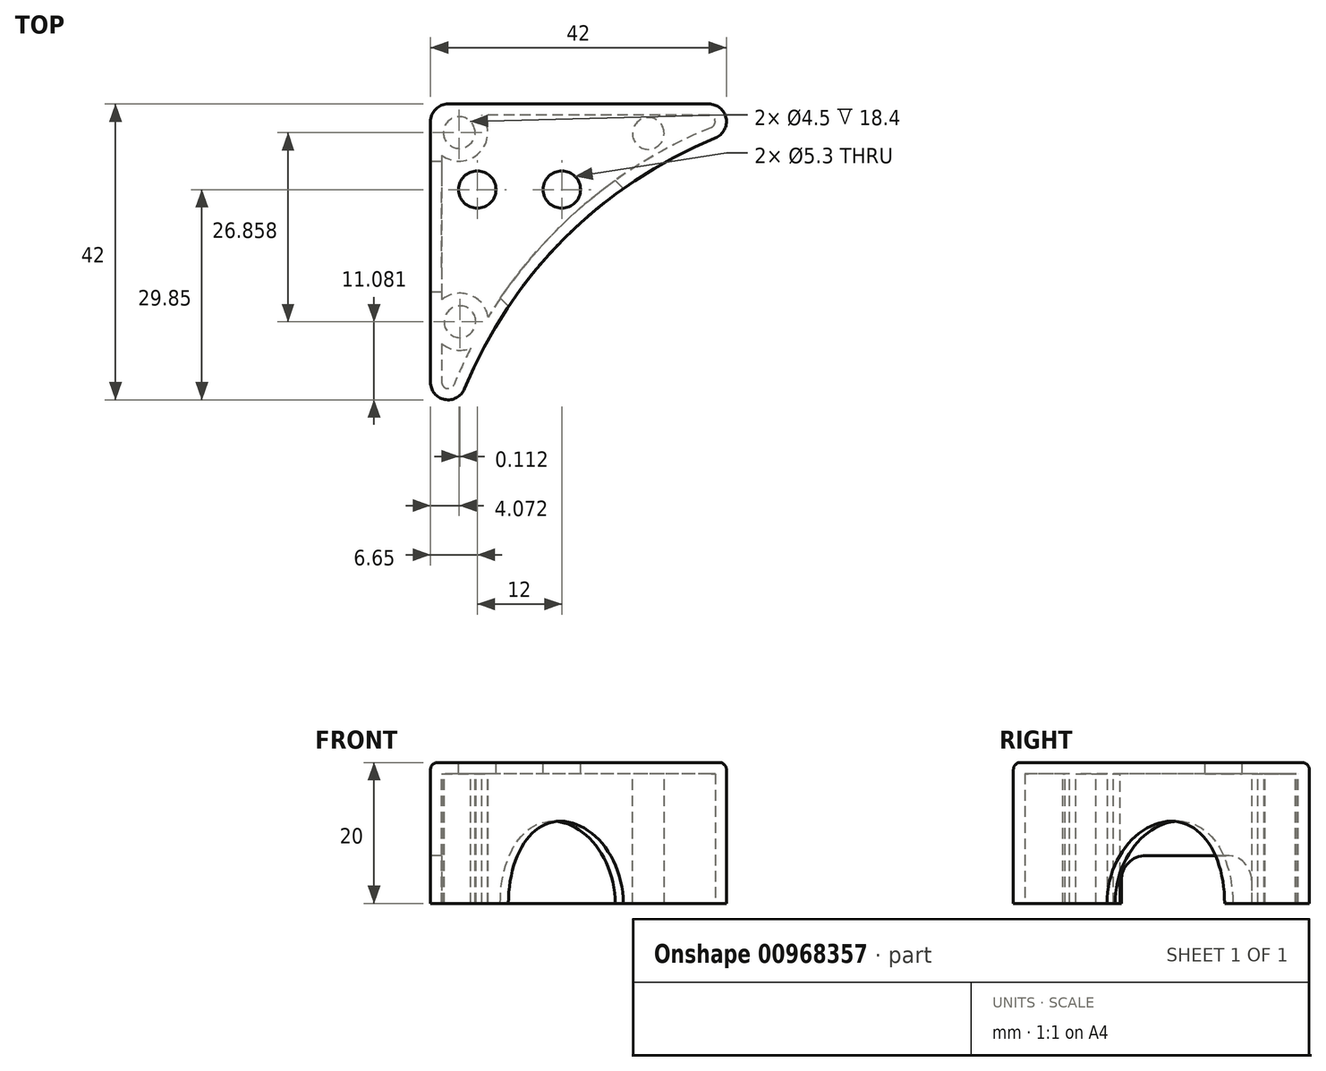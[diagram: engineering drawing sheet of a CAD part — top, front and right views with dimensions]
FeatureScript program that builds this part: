
annotation { "Feature Type Name" : "Feature", "Feature Type Description" : "" }
export const myFeature = defineFeature(function(context is Context, id is Id, definition is map)
    precondition{}
    {
        {
            var Q0;
            Q0=qCreatedBy(makeId("Top.planeOp"),FACE);
            var sketch = newSketch(context, id + "F0", { "sketchPlane" : qUnion([Q0])});
            skCircle(sketch, "E0", {"center": v(0, 0) * mm, "radius": 65 * mm});
            skLineSegment(sketch, "E1", {"start": v(0, 0) * mm, "end": v(0, 65) * mm, "construction": true});
            skLineSegment(sketch, "E2", {"start": v(0, 0) * mm, "end": v(-45.96, 45.96) * mm, "construction": true});
            skLineSegment(sketch, "E3.bottom", {"start": v(0, 65) * mm, "end": v(-65, 65) * mm});
            skLineSegment(sketch, "E3.top", {"start": v(0, 0) * mm, "end": v(-65, 0) * mm});
            skLineSegment(sketch, "E3.left", {"start": v(0, 65) * mm, "end": v(0, 0) * mm});
            skLineSegment(sketch, "E3.right", {"start": v(-65, 65) * mm, "end": v(-65, 0) * mm});
            skLineSegment(sketch, "E4.bottom", {"start": v(-65, 60) * mm, "end": v(-60, 60) * mm, "construction": true});
            skLineSegment(sketch, "E4.top", {"start": v(-65, 41.2) * mm, "end": v(-60, 41.2) * mm, "construction": true});
            skLineSegment(sketch, "E4.left", {"start": v(-65, 60) * mm, "end": v(-65, 41.2) * mm});
            skLineSegment(sketch, "E4.right", {"start": v(-60, 60) * mm, "end": v(-60, 41.2) * mm, "construction": true});
            skCircle(sketch, "E5", {"center": v(-45.96, 45.96) * mm, "radius": 5 * mm, "construction": true});
            skLineSegment(sketch, "E6", {"start": v(-65, 0) * mm, "end": v(0, 65) * mm});
            skSolve(sketch);
        }
        {
            var Q0;
            {var subQ4=sQuery(id+"F0.wireOp",EDGE,"E3.bottom");Q0=makeQuery(id+"F0.imprint","IMPRINT",FACE,{"disambiguationData":[TD([[makeQuery(id+"F0.imprint","IMPRINT",EDGE,{"derivedFrom":subQ4}),1.0]])]});}
            extrude(context, id + "F1", {"entities" : qUnion([Q0]), "depth" : 20 * mm, "offsetDistance" : 25 * mm});
        }
        {
            var Q0;
            Q0=makeQuery(id+"F1.opExtrude","SWEPT_EDGE",EDGE,{"disambiguationData":[OSD([sQuery(id+"F0.wireOp",EDGE,"E0"),sQuery(id+"F0.wireOp",EDGE,"E3.top"),sQuery(id+"F0.wireOp",EDGE,"E3.right")])]});
            var Q1;
            Q1=makeQuery(id+"F1.opExtrude","SWEPT_EDGE",EDGE,{"disambiguationData":[OSD([sQuery(id+"F0.wireOp",EDGE,"E0"),sQuery(id+"F0.wireOp",EDGE,"E3.bottom"),sQuery(id+"F0.wireOp",EDGE,"E3.left")])]});
            var Q2;
            Q2=makeQuery(id+"F1.opExtrude","SWEPT_EDGE",EDGE,{"disambiguationData":[OSD([sQuery(id+"F0.wireOp",EDGE,"E3.bottom"),sQuery(id+"F0.wireOp",EDGE,"E3.right")])]});
            fillet(context, id + "F2", {"entities" : qUnion([Q0, Q1, Q2]), "radius" : 2.5 * mm, "tangentPropagation" : true, "allowEdgeOverflow" : false});
        }
        {
            var Q0;
            Q0=makeQuery(id+"F1.opExtrude","CAP_FACE",FACE,{"disambiguationData":[OSD([sQuery(id+"F0.wireOp",EDGE,"E0"),sQuery(id+"F0.wireOp",EDGE,"E3.bottom"),sQuery(id+"F0.wireOp",EDGE,"E3.right"),sQuery(id+"F0.wireOp",EDGE,"E4.left")])],"isStart":true});
            var Q1;
            Q1=makeQuery(id+"F1.opExtrude","SWEPT_BODY",BODY,{"disambiguationData":[OSD([sQuery(id+"F0.wireOp",EDGE,"E0"),sQuery(id+"F0.wireOp",EDGE,"E3.bottom"),sQuery(id+"F0.wireOp",EDGE,"E3.right"),sQuery(id+"F0.wireOp",EDGE,"E4.left")])]});
            shell(context, id + "F3", {"entities" : qUnion([Q0]), "parts" : qUnion([Q1]), "thickness" : 1.6 * mm});
        }
        {
            var Q0;
            Q0=makeQuery(id+"F1.opExtrude","CAP_FACE",FACE,{"disambiguationData":[OSD([sQuery(id+"F0.wireOp",EDGE,"E0"),sQuery(id+"F0.wireOp",EDGE,"E3.bottom"),sQuery(id+"F0.wireOp",EDGE,"E3.right"),sQuery(id+"F0.wireOp",EDGE,"E4.left")])],"isStart":false});
            var sketch = newSketch(context, id + "F4", { "sketchPlane" : qUnion([Q0])});
            skCircle(sketch, "E7", {"center": v(-60.93, 60.94) * mm, "radius": 2.25 * mm});
            skLineSegment(sketch, "E8.0", {"start": v(-65, 65) * mm, "end": v(-65, 0) * mm, "construction": true});
            skLineSegment(sketch, "E9.0", {"start": v(0, 65) * mm, "end": v(-65, 65) * mm, "construction": true});
            skLineSegment(sketch, "E10", {"start": v(-45.96, 45.96) * mm, "end": v(-65, 65) * mm, "construction": true});
            skCircle(sketch, "E11.0", {"center": v(-60.93, 60.94) * mm, "radius": 4.05 * mm});
            skLineSegment(sketch, "E12", {"start": v(-60.34, 36.48) * mm, "end": v(-62.98, 23.04) * mm, "construction": true});
            skPoint(sketch, "E13.orphan", {"position": v(-62.5, 25.5) * mm});
            skCircle(sketch, "E14", {"center": v(-60.82, 34.08) * mm, "radius": 2.25 * mm});
            skCircle(sketch, "E15.0", {"center": v(-60.82, 34.08) * mm, "radius": 4.05 * mm});
            skCircle(sketch, "E16.MirrorC", {"center": v(-34.08, 60.82) * mm, "radius": 4.05 * mm});
            skCircle(sketch, "E17.MirrorC", {"center": v(-34.08, 60.82) * mm, "radius": 2.25 * mm});
            skLineSegment(sketch, "E18", {"start": v(-34.08, 56.77) * mm, "end": v(-32.44, 56.77) * mm, "construction": true});
            skLineSegment(sketch, "E19", {"start": v(-32.44, 56.77) * mm, "end": v(-64.37, 56.77) * mm, "construction": true});
            skCircle(sketch, "E20", {"center": v(-58.35, 52.85) * mm, "radius": 2.65 * mm});
            skCircle(sketch, "E21", {"center": v(-46.35, 52.85) * mm, "radius": 2.65 * mm});
            skSolve(sketch);
        }
        {
            var Q0;
            Q0=makeQuery(id+"F4.imprint","IMPRINT",FACE,{"disambiguationData":[TD([[makeQuery(id+"F4.imprint","IMPRINT",EDGE,{"derivedFrom":sQuery(id+"F4.wireOp",EDGE,"E7")}),-1.0]])]});
            var Q1;
            Q1=makeQuery(id+"F4.imprint","IMPRINT",FACE,{"disambiguationData":[TD([[makeQuery(id+"F4.imprint","IMPRINT",EDGE,{"derivedFrom":sQuery(id+"F4.wireOp",EDGE,"E14")}),-1.0]])]});
            var Q2;
            Q2=makeQuery(id+"F4.imprint","IMPRINT",FACE,{"disambiguationData":[TD([[makeQuery(id+"F4.imprint","IMPRINT",EDGE,{"derivedFrom":sQuery(id+"F4.wireOp",EDGE,"E17.MirrorC")}),1.0]])]});
            extrude(context, id + "F5", {"entities" : qUnion([Q0, Q1, Q2]), "operationType" : NewBodyOperationType.ADD, "oppositeDirection" : true, "depth" : 20 * mm, "offsetDistance" : 25 * mm});
        }
        {
            var Q0;
            Q0=makeQuery(id+"F1.opExtrude","SWEPT_FACE",FACE,{"disambiguationData":[OSD([sQuery(id+"F0.wireOp",EDGE,"E3.right"),sQuery(id+"F0.wireOp",EDGE,"E4.left")])]});
            var sketch = newSketch(context, id + "F6", { "sketchPlane" : qUnion([Q0])});
            skLineSegment(sketch, "E22.bottom", {"start": v(-56.8, 0) * mm, "end": v(-38.3, 0) * mm});
            skLineSegment(sketch, "E22.top", {"start": v(-56.8, 6.8) * mm, "end": v(-38.3, 6.8) * mm});
            skLineSegment(sketch, "E22.left", {"start": v(-56.8, 0) * mm, "end": v(-56.8, 6.8) * mm});
            skLineSegment(sketch, "E22.right", {"start": v(-38.3, 0) * mm, "end": v(-38.3, 6.8) * mm});
            skSolve(sketch);
        }
        {
            var Q0;
            Q0=makeQuery(id+"F6.imprint","IMPRINT",FACE,{"disambiguationData":[TD([[makeQuery(id+"F6.imprint","IMPRINT",EDGE,{"derivedFrom":sQuery(id+"F6.wireOp",EDGE,"E22.bottom")}),1.0]])]});
            extrude(context, id + "F7", {"entities" : qUnion([Q0]), "operationType" : NewBodyOperationType.REMOVE, "oppositeDirection" : true, "depth" : 7.7 * mm, "offsetDistance" : 25 * mm});
        }
        {
            var Q0;
            Q0=qCreatedBy(makeId("Right.planeOp"),FACE);
            var Q1;
            Q1=sQuery(id+"F0.wireOp",EDGE,"E6");
            cPlane(context, id + "F8", {"entities" : qUnion([Q0, Q1]), "cplaneType" : CPlaneType.LINE_ANGLE, "offset" : 25 * mm, "angle" : 0 * degree, "width" : 150 * mm, "height" : 150 * mm});
        }
        {
            var Q0;
            Q0=qCreatedBy(id+"F8.planeOp",FACE);
            var sketch = newSketch(context, id + "F9", { "sketchPlane" : qUnion([Q0])});
            skCircle(sketch, "E23", {"center": v(0.82, 0) * mm, "radius": 11.67 * mm});
            skSolve(sketch);
        }
        {
            var Q0;
            Q0=makeQuery(id+"F9.imprint","IMPRINT",FACE,{"disambiguationData":[TD([[makeQuery(id+"F9.imprint","IMPRINT",EDGE,{"derivedFrom":sQuery(id+"F9.wireOp",EDGE,"E23")}),1.0]])]});
            extrude(context, id + "F10", {"entities" : qUnion([Q0]), "operationType" : NewBodyOperationType.REMOVE, "depth" : 24.5 * mm, "offsetDistance" : 25 * mm});
        }
        {
            var Q0;
            Q0=makeQuery(id+"F7.boolean.opBoolean","COPY",EDGE,{"derivedFrom":makeQuery(id+"F7.opExtrude","SWEPT_EDGE",EDGE,{"disambiguationData":[OSD([sQuery(id+"F6.wireOp",EDGE,"E22.top"),sQuery(id+"F6.wireOp",EDGE,"E22.right")])]})});
            var Q1;
            Q1=makeQuery(id+"F7.boolean.opBoolean","COPY",EDGE,{"derivedFrom":makeQuery(id+"F7.opExtrude","SWEPT_EDGE",EDGE,{"disambiguationData":[OSD([sQuery(id+"F6.wireOp",EDGE,"E22.top"),sQuery(id+"F6.wireOp",EDGE,"E22.left")])]})});
            fillet(context, id + "F11", {"entities" : qUnion([Q0, Q1]), "radius" : 3.5 * mm, "tangentPropagation" : true, "allowEdgeOverflow" : false});
        }
        {
            var Q0;
            Q0=makeQuery(id+"F1.opExtrude","CAP_EDGE",EDGE,{"disambiguationData":[OSD([sQuery(id+"F0.wireOp",EDGE,"E0")])],"isStart":false});
            var Q1;
            {var subQ0=sQuery(id+"F0.wireOp",EDGE,"E3.bottom");var subQ1=sQuery(id+"F0.wireOp",EDGE,"E0");Q1=makeQuery(id+"F2.opFillet","BLEND_EDGE",EDGE,{"blendedFrom":[makeQuery(id+"F1.opExtrude","SWEPT_EDGE",EDGE,{"disambiguationData":[OSD([subQ1,subQ0,sQuery(id+"F0.wireOp",EDGE,"E3.left"),sQuery(id+"F0.wireOp",EDGE,"E6")])]}),makeQuery(id+"F1.opExtrude","CAP_FACE",FACE,{"disambiguationData":[OSD([subQ1,subQ0,sQuery(id+"F0.wireOp",EDGE,"E3.right"),sQuery(id+"F0.wireOp",EDGE,"E4.left")])],"isStart":false})],"blendedInto":[makeQuery(id+"F1.opExtrude","CAP_FACE",FACE,{"disambiguationData":[OSD([subQ1,subQ0,sQuery(id+"F0.wireOp",EDGE,"E3.right"),sQuery(id+"F0.wireOp",EDGE,"E4.left")])],"isStart":false})]});}
            var Q2;
            Q2=makeQuery(id+"F1.opExtrude","CAP_EDGE",EDGE,{"disambiguationData":[OSD([sQuery(id+"F0.wireOp",EDGE,"E3.bottom")])],"isStart":false});
            var Q3;
            {var subQ0=sQuery(id+"F0.wireOp",EDGE,"E3.right");var subQ1=sQuery(id+"F0.wireOp",EDGE,"E0");Q3=makeQuery(id+"F2.opFillet","BLEND_EDGE",EDGE,{"blendedFrom":[makeQuery(id+"F1.opExtrude","SWEPT_EDGE",EDGE,{"disambiguationData":[OSD([subQ1,sQuery(id+"F0.wireOp",EDGE,"E3.top"),subQ0,sQuery(id+"F0.wireOp",EDGE,"E6")])]}),makeQuery(id+"F1.opExtrude","CAP_FACE",FACE,{"disambiguationData":[OSD([subQ1,sQuery(id+"F0.wireOp",EDGE,"E3.bottom"),subQ0,sQuery(id+"F0.wireOp",EDGE,"E4.left")])],"isStart":false})],"blendedInto":[makeQuery(id+"F1.opExtrude","CAP_FACE",FACE,{"disambiguationData":[OSD([subQ1,sQuery(id+"F0.wireOp",EDGE,"E3.bottom"),subQ0,sQuery(id+"F0.wireOp",EDGE,"E4.left")])],"isStart":false})]});}
            var Q4;
            Q4=makeQuery(id+"F1.opExtrude","CAP_EDGE",EDGE,{"disambiguationData":[OSD([sQuery(id+"F0.wireOp",EDGE,"E3.right"),sQuery(id+"F0.wireOp",EDGE,"E4.left")])],"isStart":false});
            fillet(context, id + "F12", {"entities" : qUnion([Q0, Q1, Q2, Q3, Q4]), "radius" : 1 * mm, "tangentPropagation" : true, "allowEdgeOverflow" : false});
        }
        {
            var Q0;
            Q0=makeQuery(id+"F4.imprint","IMPRINT",FACE,{"disambiguationData":[TD([[makeQuery(id+"F4.imprint","IMPRINT",EDGE,{"derivedFrom":sQuery(id+"F4.wireOp",EDGE,"E20")}),1.0]])]});
            var Q1;
            Q1=makeQuery(id+"F4.imprint","IMPRINT",FACE,{"disambiguationData":[TD([[makeQuery(id+"F4.imprint","IMPRINT",EDGE,{"derivedFrom":sQuery(id+"F4.wireOp",EDGE,"E21")}),1.0]])]});
            extrude(context, id + "F13", {"entities" : qUnion([Q0, Q1]), "operationType" : NewBodyOperationType.REMOVE, "oppositeDirection" : true, "depth" : 25 * mm, "offsetDistance" : 25 * mm});
        }
    });
